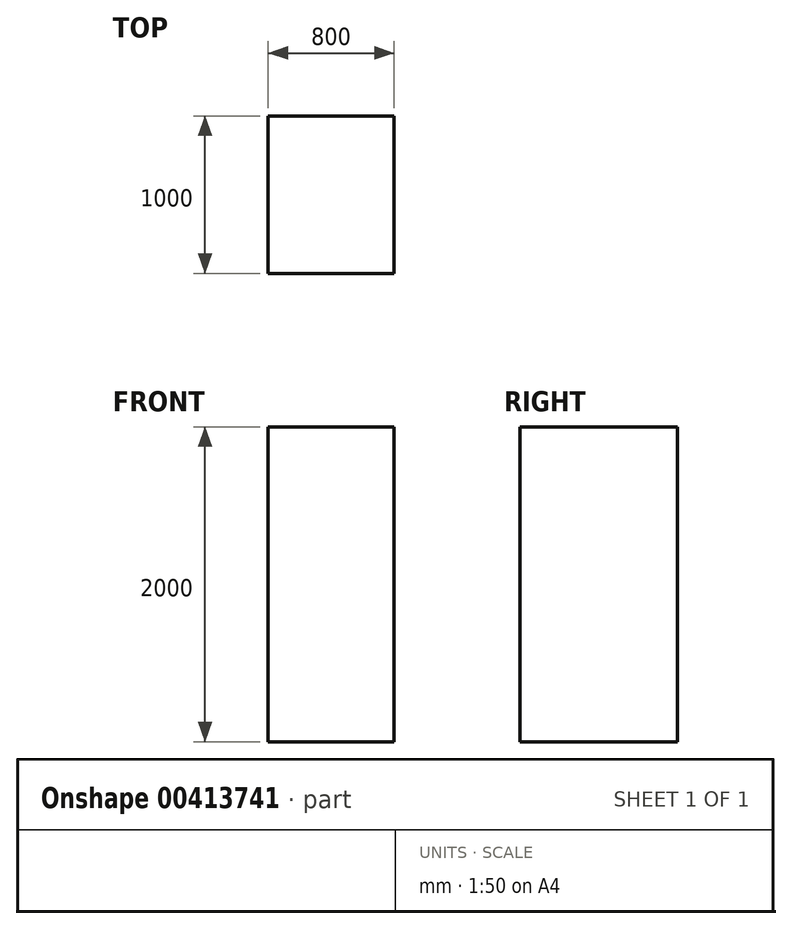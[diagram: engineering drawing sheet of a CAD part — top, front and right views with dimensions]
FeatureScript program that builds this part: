
annotation { "Feature Type Name" : "Feature", "Feature Type Description" : "" }
export const myFeature = defineFeature(function(context is Context, id is Id, definition is map)
    precondition{}
    {
        {
            var Q0;
            Q0=qCreatedBy(makeId("Front.planeOp"),FACE);
            var sketch = newSketch(context, id + "F0", { "sketchPlane" : qUnion([Q0])});
            skLineSegment(sketch, "E0.bottom", {"start": v(-400, 1000) * mm, "end": v(400, 1000) * mm});
            skLineSegment(sketch, "E0.top", {"start": v(-400, -1000) * mm, "end": v(400, -1000) * mm});
            skLineSegment(sketch, "E0.left", {"start": v(-400, 1000) * mm, "end": v(-400, -1000) * mm});
            skLineSegment(sketch, "E0.right", {"start": v(400, 1000) * mm, "end": v(400, -1000) * mm});
            skPoint(sketch, "E0.middle", {"position": v(0, 0) * mm});
            skSolve(sketch);
        }
        {
            var Q0;
            Q0=makeQuery(id+"F0.imprint","IMPRINT",FACE,{"disambiguationData":[TD([[makeQuery(id+"F0.imprint","IMPRINT",EDGE,{"derivedFrom":sQuery(id+"F0.wireOp",EDGE,"E0.bottom")}),-1.0]])]});
            var Q1;
            Q1=sQuery(id+"F0.wireOp",EDGE,"E0.right");
            extrude(context, id + "F1", {"entities" : qUnion([Q0]), "surfaceEntities" : qUnion([Q1]), "depth" : 1000 * mm});
        }
    });
